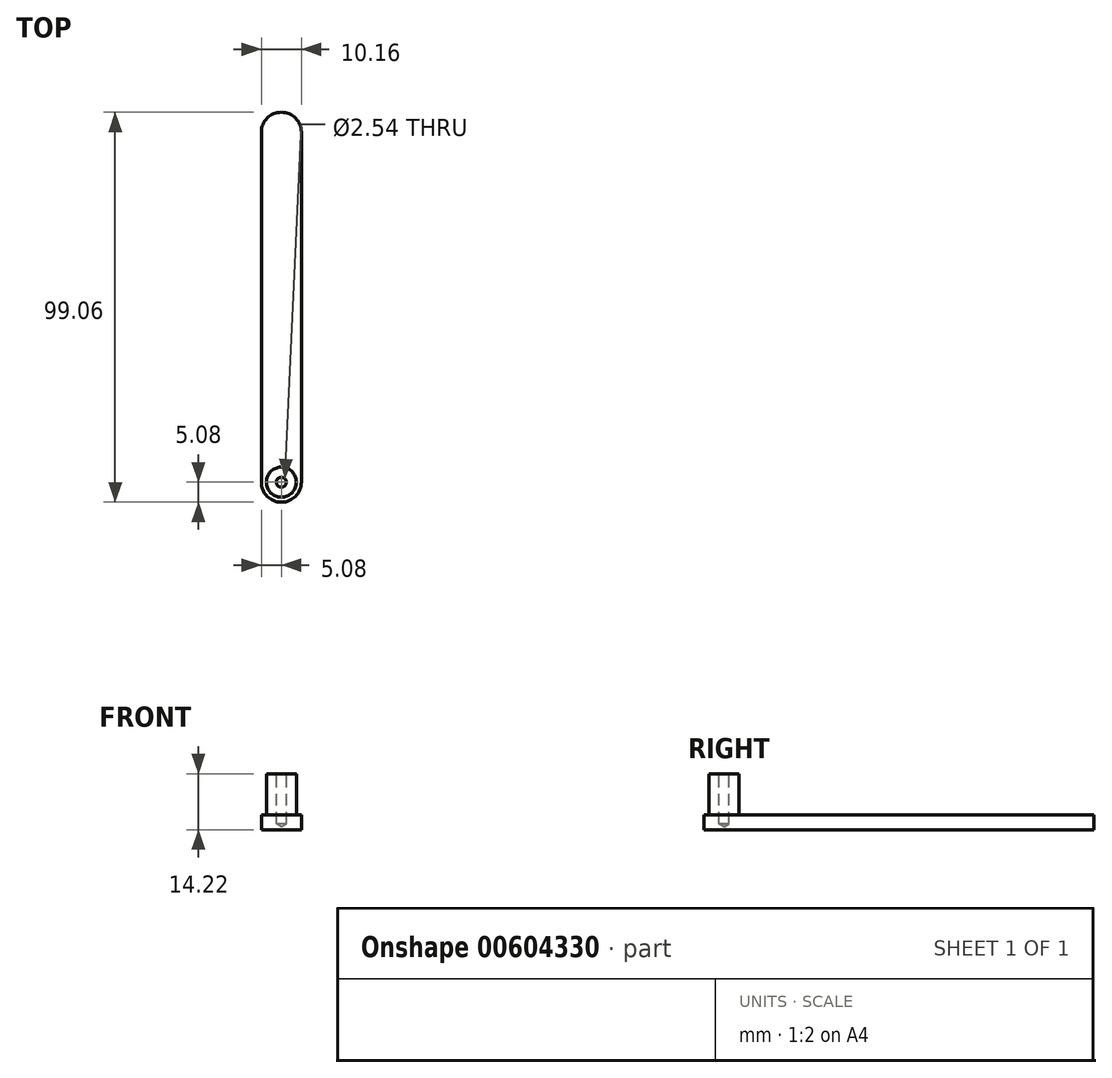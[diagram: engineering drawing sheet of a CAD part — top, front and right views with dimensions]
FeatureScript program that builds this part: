
annotation { "Feature Type Name" : "Feature", "Feature Type Description" : "" }
export const myFeature = defineFeature(function(context is Context, id is Id, definition is map)
    precondition{}
    {
        {
            var Q0;
            Q0=qCreatedBy(makeId("Top.planeOp"),FACE);
            var sketch = newSketch(context, id + "F0", { "sketchPlane" : qUnion([Q0])});
            skArc(sketch, "E0", {"start": v(0, 5.08) * mm, "mid": v(5.08, 0) * mm, "end": v(10.16, 5.08) * mm});
            skArc(sketch, "E1", {"start": v(10.16, 93.98) * mm, "mid": v(5.08, 99.06) * mm, "end": v(0, 93.98) * mm});
            skLineSegment(sketch, "E2", {"start": v(0, 93.98) * mm, "end": v(0, 5.08) * mm});
            skLineSegment(sketch, "E3", {"start": v(10.16, 93.98) * mm, "end": v(10.16, 5.08) * mm});
            skSolve(sketch);
        }
        {
            var Q0;
            Q0 = qSketchRegion(id + "F0", true);
            extrude(context, id + "F1", {"entities" : qUnion([Q0]), "depth" : 3.8 * mm, "offsetDistance" : 25.4 * mm});
        }
        {
            var Q0;
            Q0=makeQuery(id+"F1.opExtrude","CAP_FACE",FACE,{"disambiguationData":[OSD([sQuery(id+"F0.wireOp",EDGE,"E0"),sQuery(id+"F0.wireOp",EDGE,"E1"),sQuery(id+"F0.wireOp",EDGE,"E2"),sQuery(id+"F0.wireOp",EDGE,"E3")])],"isStart":false});
            var sketch = newSketch(context, id + "F2", { "sketchPlane" : qUnion([Q0])});
            skCircle(sketch, "E4", {"center": v(5.08, 5.08) * mm, "radius": 3.8 * mm});
            skSolve(sketch);
        }
        {
            var Q0;
            Q0 = qSketchRegion(id + "F2", true);
            extrude(context, id + "F3", {"entities" : qUnion([Q0]), "operationType" : NewBodyOperationType.ADD, "depth" : 10.4 * mm, "offsetDistance" : 25.4 * mm});
        }
        {
            var Q0;
            Q0=makeQuery(id+"F3.opExtrude","CAP_FACE",FACE,{"disambiguationData":[OSD([sQuery(id+"F2.wireOp",EDGE,"E4")])],"isStart":false});
            var sketch = newSketch(context, id + "F4", { "sketchPlane" : qUnion([Q0])});
            skPoint(sketch, "E5", {"position": v(5.08, 5.08) * mm});
            skSolve(sketch);
        }
        {
            var Q0;
            Q0=sQuery(id+"F4.wireOp",VERTEX,"E5");
            var Q1;
            Q1=makeQuery(id+"F1.opExtrude","SWEPT_BODY",BODY,{"disambiguationData":[OSD([sQuery(id+"F0.wireOp",EDGE,"E0"),sQuery(id+"F0.wireOp",EDGE,"E1"),sQuery(id+"F0.wireOp",EDGE,"E2"),sQuery(id+"F0.wireOp",EDGE,"E3")])]});
            hole(context, id + "F5", {"style" : HoleStyle.SIMPLE, "endStyle" : HoleEndStyle.BLIND, "holeDiameter" : 2.54 * mm, "majorDiameter" : 6.35 * mm, "holeDepth" : 12.7 * mm, "isTappedThrough" : true, "tappedDepth" : 12.7 * mm, "tapClearance" : 3, "startFromSketch" : true, "locations" : qUnion([Q0]), "scope" : qUnion([Q1])});
        }
    });
